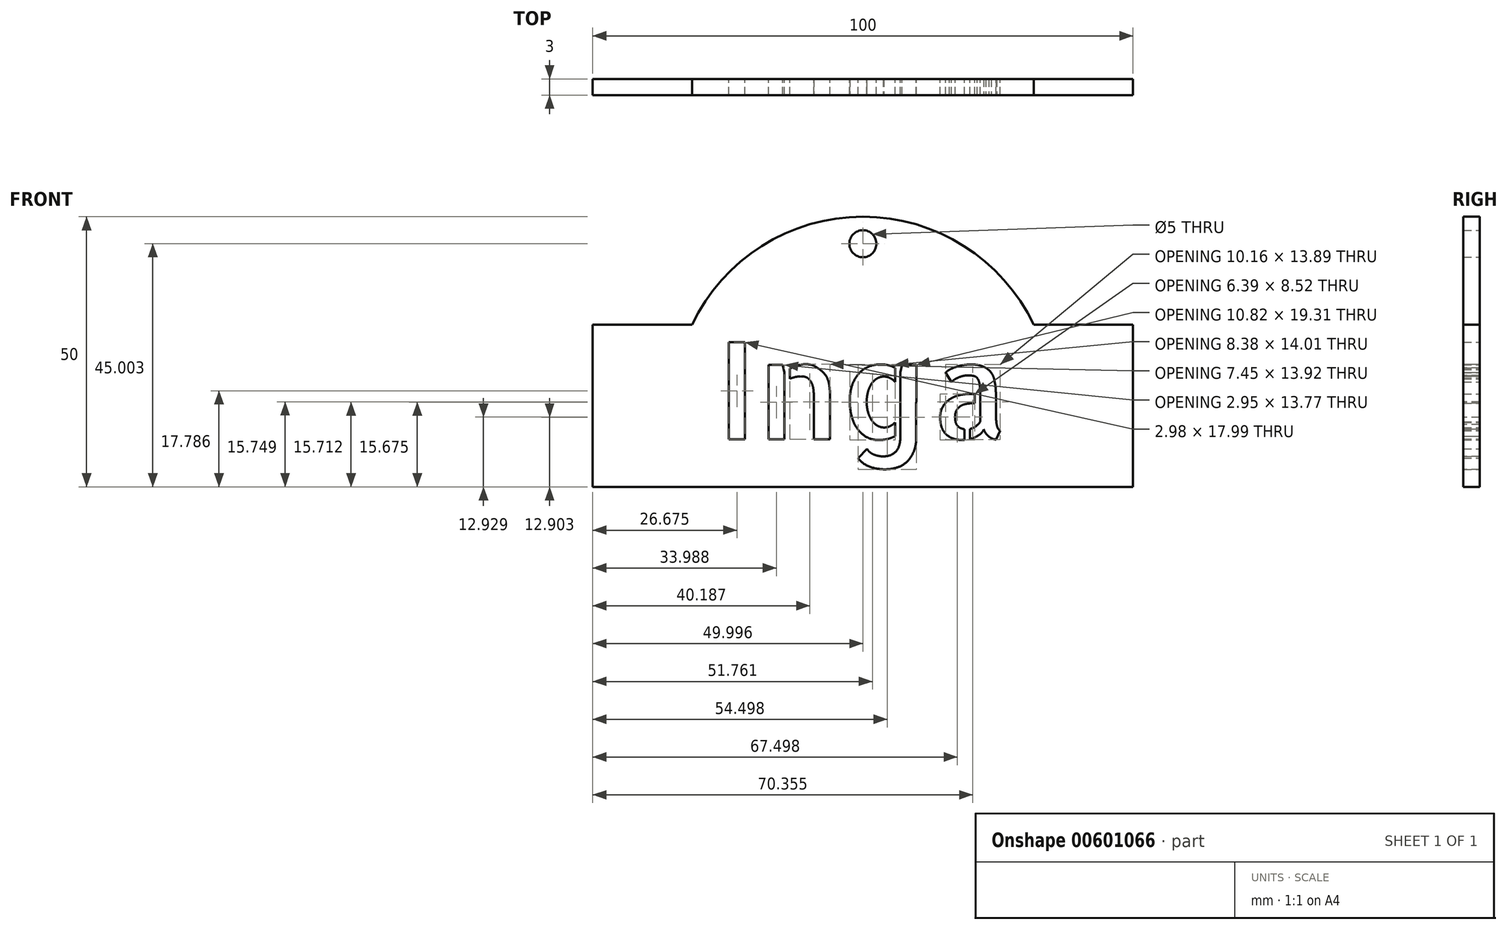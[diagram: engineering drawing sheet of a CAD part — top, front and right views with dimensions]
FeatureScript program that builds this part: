
annotation { "Feature Type Name" : "Feature", "Feature Type Description" : "" }
export const myFeature = defineFeature(function(context is Context, id is Id, definition is map)
    precondition{}
    {
        {
            var Q0;
            Q0=qCreatedBy(makeId("Front.planeOp"),FACE);
            var sketch = newSketch(context, id + "F0", { "sketchPlane" : qUnion([Q0])});
            skLineSegment(sketch, "E0.bottom", {"start": v(-117.91, -41.86) * mm, "end": v(-99.54, -41.86) * mm});
            skLineSegment(sketch, "E0.top", {"start": v(-117.91, -71.86) * mm, "end": v(-17.91, -71.86) * mm});
            skLineSegment(sketch, "E0.left", {"start": v(-117.91, -41.86) * mm, "end": v(-117.91, -71.86) * mm});
            skLineSegment(sketch, "E0.right", {"start": v(-17.91, -41.86) * mm, "end": v(-17.91, -71.86) * mm});
            skArc(sketch, "E1", {"start": v(-99.54, -41.86) * mm, "mid": v(-67.91, -21.86) * mm, "end": v(-36.3, -41.86) * mm});
            skCircle(sketch, "E2", {"center": v(-67.91, -26.86) * mm, "radius": 2.5 * mm});
            skPoint(sketch, "E3", {"position": v(-67.91, -41.86) * mm});
            skPoint(sketch, "E4", {"position": v(-17.91, -56.86) * mm});
            skPoint(sketch, "E5", {"position": v(-67.91, -71.86) * mm});
            skText(sketch, "E6", { "text": "Inga", "fontName": "AllertaStencil-Regular.ttf"});
            skLineSegment(sketch, "E7.trimOffspring", {"start": v(-36.3, -41.86) * mm, "end": v(-17.91, -41.86) * mm});
            const initialGuessF0  = {"E6": [-0.09502, -0.06307, 1, 0, 0.018]};
            skSetInitialGuess(sketch, initialGuessF0);
            skSolve(sketch);
        }
        {
            var Q0;
            Q0=makeQuery(id+"F0.imprint","IMPRINT",FACE,{"disambiguationData":[TD([[makeQuery(id+"F0.imprint","IMPRINT",EDGE,{"derivedFrom":sQuery(id+"F0.wireOp",EDGE,"E0.bottom")}),-1.0]])]});
            extrude(context, id + "F1", {"entities" : qUnion([Q0]), "depth" : 3 * mm, "offsetDistance" : 25 * mm});
        }
    });
